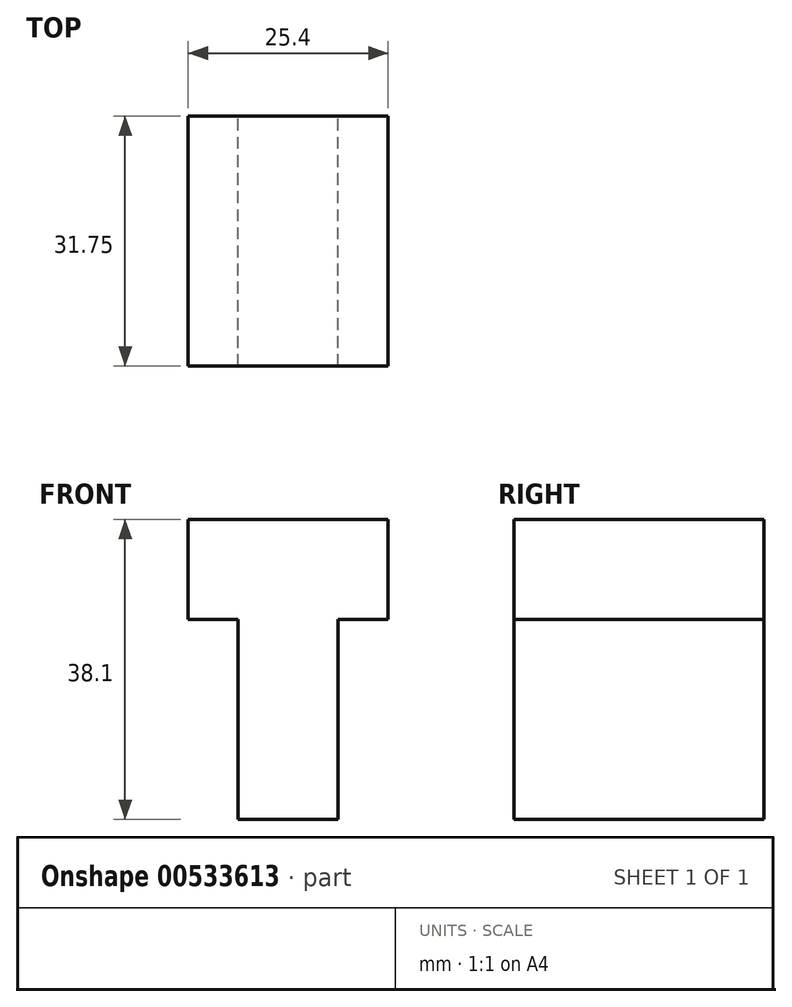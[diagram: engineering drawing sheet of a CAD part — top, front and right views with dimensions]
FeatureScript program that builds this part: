
annotation { "Feature Type Name" : "Feature", "Feature Type Description" : "" }
export const myFeature = defineFeature(function(context is Context, id is Id, definition is map)
    precondition{}
    {
        {
            var Q0;
            Q0=qCreatedBy(makeId("Front.planeOp"),FACE);
            var sketch = newSketch(context, id + "F0", { "sketchPlane" : qUnion([Q0])});
            skLineSegment(sketch, "E0", {"start": v(-50.98, 40.81) * mm, "end": v(-50.98, 15.41) * mm});
            skLineSegment(sketch, "E1", {"start": v(-50.98, 15.41) * mm, "end": v(-38.28, 15.41) * mm});
            skLineSegment(sketch, "E2", {"start": v(-38.28, 15.41) * mm, "end": v(-38.28, 40.81) * mm});
            skLineSegment(sketch, "E3", {"start": v(-38.28, 40.81) * mm, "end": v(-31.93, 40.81) * mm});
            skLineSegment(sketch, "E4", {"start": v(-31.93, 40.81) * mm, "end": v(-31.93, 53.51) * mm});
            skLineSegment(sketch, "E5", {"start": v(-31.93, 53.51) * mm, "end": v(-57.33, 53.51) * mm});
            skLineSegment(sketch, "E6", {"start": v(-57.33, 53.51) * mm, "end": v(-57.33, 40.81) * mm});
            skLineSegment(sketch, "E7", {"start": v(-57.33, 40.81) * mm, "end": v(-50.98, 40.81) * mm});
            skSolve(sketch);
        }
        {
            var Q0;
            Q0=makeQuery(id+"F0.imprint","IMPRINT",FACE,{"disambiguationData":[TD([[makeQuery(id+"F0.imprint","IMPRINT",EDGE,{"derivedFrom":sQuery(id+"F0.wireOp",EDGE,"E0")}),1.0]])]});
            extrude(context, id + "F1", {"entities" : qUnion([Q0]), "depth" : 31.75 * mm, "offsetDistance" : 25.4 * mm});
        }
    });
